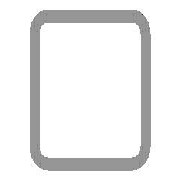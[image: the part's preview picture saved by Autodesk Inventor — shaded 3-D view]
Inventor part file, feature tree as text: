
AUTODESK INVENTOR PART (.ipt)
format: ipt  version: 2022 (Build 260153000, 153)  size: 263,680 bytes
history: native  units: mm (DEFAULTED — no unit token found)
features: other x7, sketch x3, surface_op x2, plane x1
ambient origin geometry x8: Origin, YZ Plane, XZ Plane, XY Plane, X Axis, Y Axis, Z Axis, Center Point
bodies: Solid1 (feature_tree), Body (feature_tree), Solid3 (feature_tree)
feature tree (13):
  parser-record x1  (decoder bookkeeping rows leaked as tree rows — omitted from the tree; the rows remain in map.json)
  other  "Driven Length"
  other  "Start Plane"
  other  "End Plane"
  sketch  "Sketch"  dims[d7=6.0mm d10=40.0mm d11=40.0mm d12=4.0mm d13=-0.0mm d14=180.0mm d15=20.0mm d16=20.0mm d17=90.0deg d18=180.0mm d37=5.0mm d38=5.0mm d39=5.0mm d40=5.0mm d41=5.0mm d42=5.0mm d43=5.0mm d44=5.0mm d45=0.0mm d46=5.0mm d47=5.0mm d48=5.0mm d49=5.0mm d50=5.0mm d51=5.0mm d52=5.0mm d53=5.0mm d54=0.0mm]
  sketch  "Sketch3"  dims[d3=155.0mm]
  plane  "Work Plane3"
  sketch  "Sketch4"  dims[d4=0.0mm]
  other  "Srf5"
  other  "Srf6"
  other  "Srf4"
  surface_op  "Boundary Patch3"
  surface_op  "Boundary Patch4"
